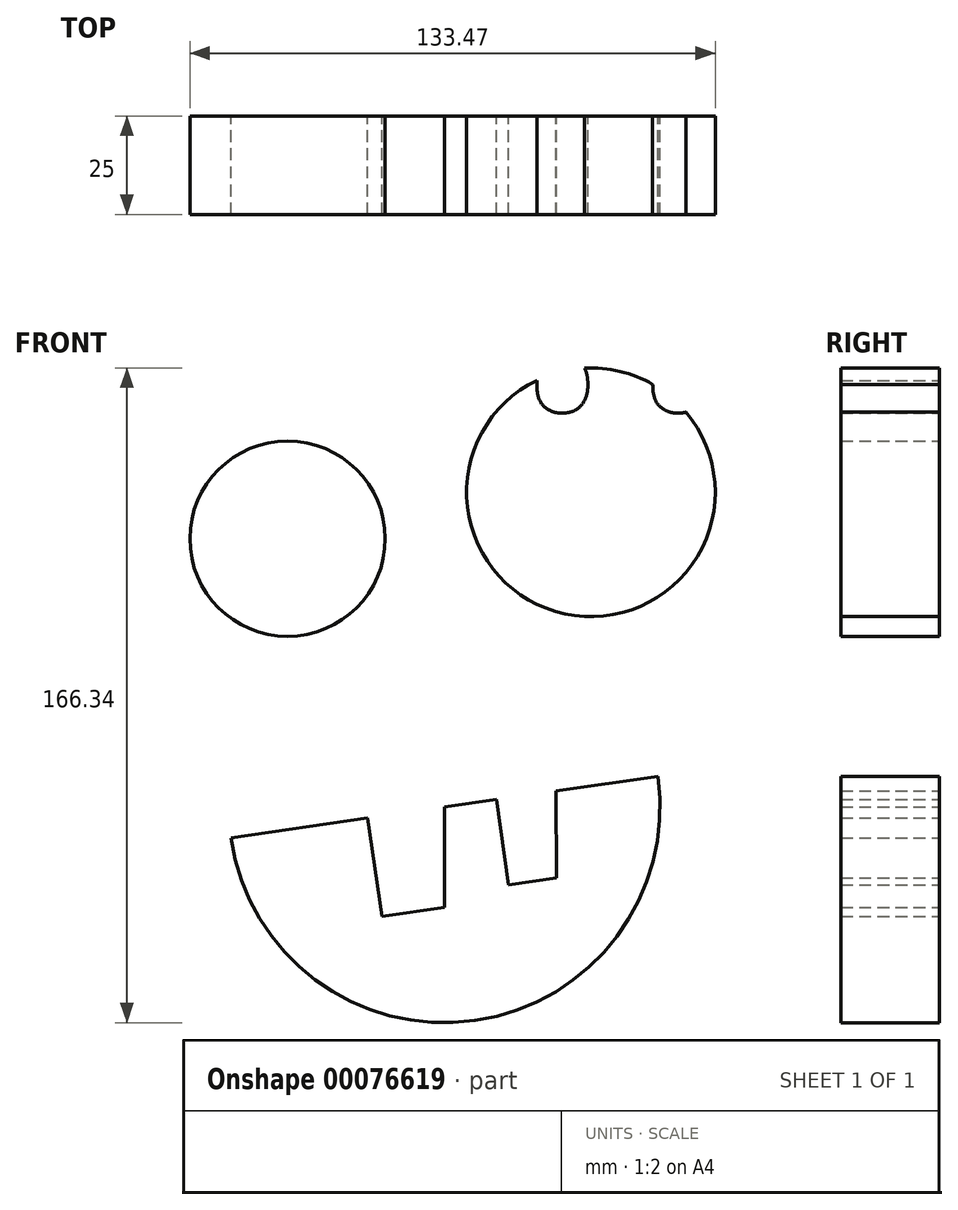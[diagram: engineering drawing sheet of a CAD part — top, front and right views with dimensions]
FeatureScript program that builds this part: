
annotation { "Feature Type Name" : "Feature", "Feature Type Description" : "" }
export const myFeature = defineFeature(function(context is Context, id is Id, definition is map)
    precondition{}
    {
        {
            var Q0;
            Q0=qCreatedBy(makeId("Front.planeOp"),FACE);
            var sketch = newSketch(context, id + "F0", { "sketchPlane" : qUnion([Q0])});
            skLineSegment(sketch, "E0.bottom", {"start": v(275.86, 162.71) * mm, "end": v(-24.14, 162.71) * mm});
            skLineSegment(sketch, "E0.top", {"start": v(275.86, 35.71) * mm, "end": v(-24.14, 35.71) * mm});
            skLineSegment(sketch, "E0.left", {"start": v(275.86, 162.71) * mm, "end": v(275.86, 35.71) * mm});
            skLineSegment(sketch, "E0.right", {"start": v(-24.14, 162.71) * mm, "end": v(-24.14, 35.71) * mm});
            skCircle(sketch, "E1", {"center": v(-24.14, 162.71) * mm, "radius": 67.82 * mm});
            skCircle(sketch, "E2", {"center": v(103.49, 219.32) * mm, "radius": 24.82 * mm});
            skCircle(sketch, "E3", {"center": v(180.56, 231.12) * mm, "radius": 31.58 * mm});
            skArc(sketch, "E4", {"start": v(89.12, 143.32) * mm, "mid": v(151.14, 96.92) * mm, "end": v(197.54, 158.95) * mm});
            skLineSegment(sketch, "E5", {"start": v(89.12, 143.32) * mm, "end": v(197.54, 158.95) * mm});
            skLineSegment(sketch, "E6", {"start": v(123.86, 148.33) * mm, "end": v(127.46, 123.39) * mm});
            skLineSegment(sketch, "E7", {"start": v(127.46, 123.39) * mm, "end": v(143.41, 125.69) * mm});
            skLineSegment(sketch, "E8", {"start": v(143.41, 125.69) * mm, "end": v(143.33, 151.14) * mm});
            skLineSegment(sketch, "E9", {"start": v(156.52, 153.04) * mm, "end": v(159.65, 131.37) * mm});
            skLineSegment(sketch, "E10", {"start": v(159.65, 131.37) * mm, "end": v(171.77, 133.12) * mm});
            skLineSegment(sketch, "E11", {"start": v(171.77, 133.12) * mm, "end": v(171.61, 158.39) * mm});
            skText(sketch, "E12", { "text": "FULT!!!!", "fontName": "OpenSans-Regular.ttf"});
            const initialGuessF0  = {"E12": [-0.12627, 0.2528, 1, 0, 0.0794]};
            skSetInitialGuess(sketch, initialGuessF0);
            skSolve(sketch);
        }
        {
            var Q0;
            {var subQ1=sQuery(id+"F0.wireOp",EDGE,"E4");Q0=makeQuery(id+"F0.imprint","IMPRINT",FACE,{"disambiguationData":[TD([[makeQuery(id+"F0.imprint","IMPRINT",EDGE,{"derivedFrom":subQ1}),1.0]])]});}
            var Q1;
            Q1=makeQuery(id+"F0.imprint","IMPRINT",FACE,{"disambiguationData":[TD([[makeQuery(id+"F0.imprint","IMPRINT",EDGE,{"derivedFrom":sQuery(id+"F0.wireOp",EDGE,"E2")}),1.0]])]});
            var Q2;
            Q2=makeQuery(id+"F0.imprint","IMPRINT",FACE,{"disambiguationData":[TD([[makeQuery(id+"F0.imprint","IMPRINT",EDGE,{"derivedFrom":sQuery(id+"F0.wireOp",EDGE,"E3")}),1.0]])]});
            extrude(context, id + "F1", {"entities" : qUnion([Q0, Q1, Q2]), "depth" : 25 * mm});
        }
    });
